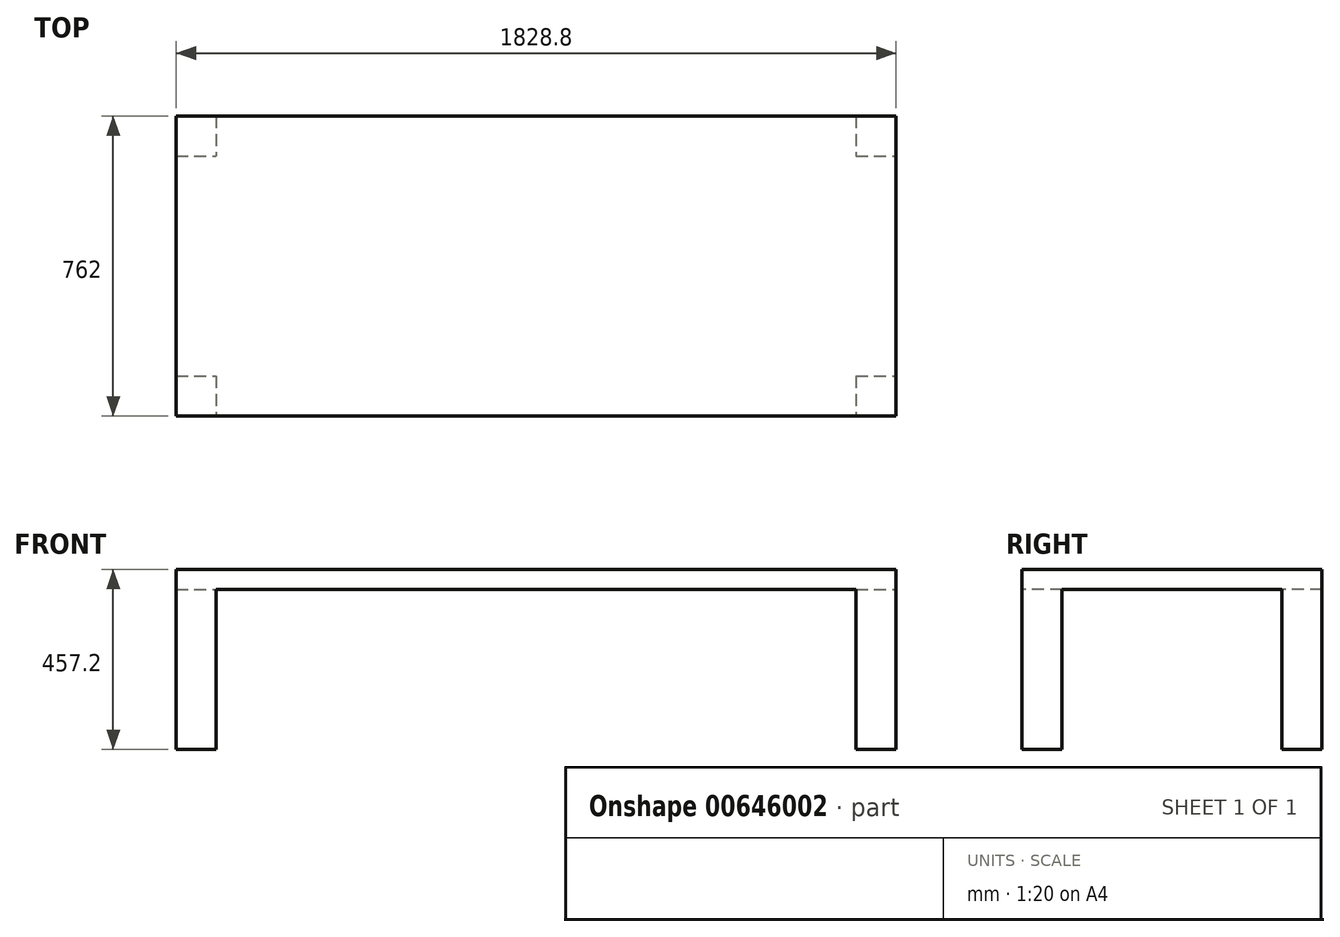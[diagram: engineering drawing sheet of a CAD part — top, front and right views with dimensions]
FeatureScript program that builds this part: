
annotation { "Feature Type Name" : "Feature", "Feature Type Description" : "" }
export const myFeature = defineFeature(function(context is Context, id is Id, definition is map)
    precondition{}
    {
        {
            var Q0;
            Q0=qCreatedBy(makeId("Top.planeOp"),FACE);
            var sketch = newSketch(context, id + "F0", { "sketchPlane" : qUnion([Q0])});
            skLineSegment(sketch, "E0.bottom", {"start": v(914.4, 381) * mm, "end": v(-914.4, 381) * mm});
            skLineSegment(sketch, "E0.top", {"start": v(914.4, -381) * mm, "end": v(-914.4, -381) * mm});
            skLineSegment(sketch, "E0.left", {"start": v(914.4, 381) * mm, "end": v(914.4, -381) * mm});
            skLineSegment(sketch, "E0.right", {"start": v(-914.4, 381) * mm, "end": v(-914.4, -381) * mm});
            skPoint(sketch, "E0.middle", {"position": v(0, 0) * mm});
            skSolve(sketch);
        }
        {
            var Q0;
            Q0=makeQuery(id+"F0.imprint","IMPRINT",FACE,{"disambiguationData":[TD([[makeQuery(id+"F0.imprint","IMPRINT",EDGE,{"derivedFrom":sQuery(id+"F0.wireOp",EDGE,"E0.bottom")}),1.0]])]});
            extrude(context, id + "F1", {"entities" : qUnion([Q0]), "depth" : 406.4 * mm, "offsetDistance" : 25.4 * mm});
        }
        {
            var Q0;
            Q0=makeQuery(id+"F1.opExtrude","SWEPT_FACE",FACE,{"disambiguationData":[OSD([sQuery(id+"F0.wireOp",EDGE,"E0.top")])]});
            var sketch = newSketch(context, id + "F2", { "sketchPlane" : qUnion([Q0])});
            skLineSegment(sketch, "E1", {"start": v(-914.4, 406.4) * mm, "end": v(-812.8, 406.4) * mm});
            skLineSegment(sketch, "E2", {"start": v(-812.8, 406.4) * mm, "end": v(-812.8, 0) * mm});
            skLineSegment(sketch, "E3", {"start": v(914.4, 406.4) * mm, "end": v(812.8, 406.4) * mm});
            skLineSegment(sketch, "E4", {"start": v(812.8, 406.4) * mm, "end": v(812.8, 0) * mm});
            skSolve(sketch);
        }
        {
            var Q0;
            Q0=makeQuery(id+"F1.opExtrude","CAP_FACE",FACE,{"disambiguationData":[OSD([sQuery(id+"F0.wireOp",EDGE,"E0.bottom"),sQuery(id+"F0.wireOp",EDGE,"E0.top"),sQuery(id+"F0.wireOp",EDGE,"E0.left"),sQuery(id+"F0.wireOp",EDGE,"E0.right")])],"isStart":false});
            extrude(context, id + "F3", {"entities" : qUnion([Q0]), "operationType" : NewBodyOperationType.ADD, "depth" : 50.8 * mm, "offsetDistance" : 25.4 * mm});
        }
        {
            var Q0;
            {var subQ0=sQuery(id+"F2.wireOp",EDGE,"E2");Q0=makeQuery(id+"F2.imprint","IMPRINT",FACE,{"disambiguationData":[TD([[makeQuery(id+"F2.imprint","IMPRINT",EDGE,{"derivedFrom":subQ0}),1.0]])]});}
            extrude(context, id + "F4", {"entities" : qUnion([Q0]), "operationType" : NewBodyOperationType.REMOVE, "oppositeDirection" : true, "depth" : 762 * mm, "offsetDistance" : 25.4 * mm});
        }
        {
            var Q0;
            {var subQ0=sQuery(id+"F0.wireOp",EDGE,"E0.left");Q0=makeQuery(id+"F3.boolean.opBoolean","MERGE",FACE,{"derivedFrom":[makeQuery(id+"F1.opExtrude","SWEPT_FACE",FACE,{"disambiguationData":[OSD([subQ0])]}),makeQuery(id+"F3.opExtrude","SWEPT_FACE",FACE,{"disambiguationData":[OSD([subQ0])]})]});}
            var sketch = newSketch(context, id + "F5", { "sketchPlane" : qUnion([Q0])});
            skLineSegment(sketch, "E5", {"start": v(-381, 457.2) * mm, "end": v(-279.4, 457.2) * mm});
            skLineSegment(sketch, "E6", {"start": v(-279.4, 457.2) * mm, "end": v(-279.4, 0) * mm});
            skLineSegment(sketch, "E7", {"start": v(381, 457.2) * mm, "end": v(279.4, 457.2) * mm});
            skLineSegment(sketch, "E8", {"start": v(279.4, 457.2) * mm, "end": v(279.4, 0) * mm});
            skLineSegment(sketch, "E9", {"start": v(381, 457.2) * mm, "end": v(381, 406.4) * mm});
            skLineSegment(sketch, "E10", {"start": v(381, 406.4) * mm, "end": v(-381, 406.4) * mm});
            skSolve(sketch);
        }
        {
            var Q0;
            {var subQ0=sQuery(id+"F5.wireOp",EDGE,"E6");var subQ1=makeQuery(id+"F1.opExtrude","CAP_EDGE",EDGE,{"disambiguationData":[OSD([sQuery(id+"F0.wireOp",EDGE,"E0.left")])],"isStart":true});var subQ2=makeQuery(id+"F5.imprint","INTERSECT",VERTEX,{"derivedFrom":[subQ1,subQ0]});Q0=makeQuery(id+"F5.imprint","IMPRINT",FACE,{"disambiguationData":[TD([[makeQuery(id+"F5.imprint","IMPRINT",EDGE,{"disambiguationData":[TD([[subQ2,1.0]])],"derivedFrom":subQ0}),1.0]])]});}
            extrude(context, id + "F6", {"entities" : qUnion([Q0]), "operationType" : NewBodyOperationType.REMOVE, "oppositeDirection" : true, "depth" : 1828.8 * mm, "offsetDistance" : 25.4 * mm});
        }
    });
